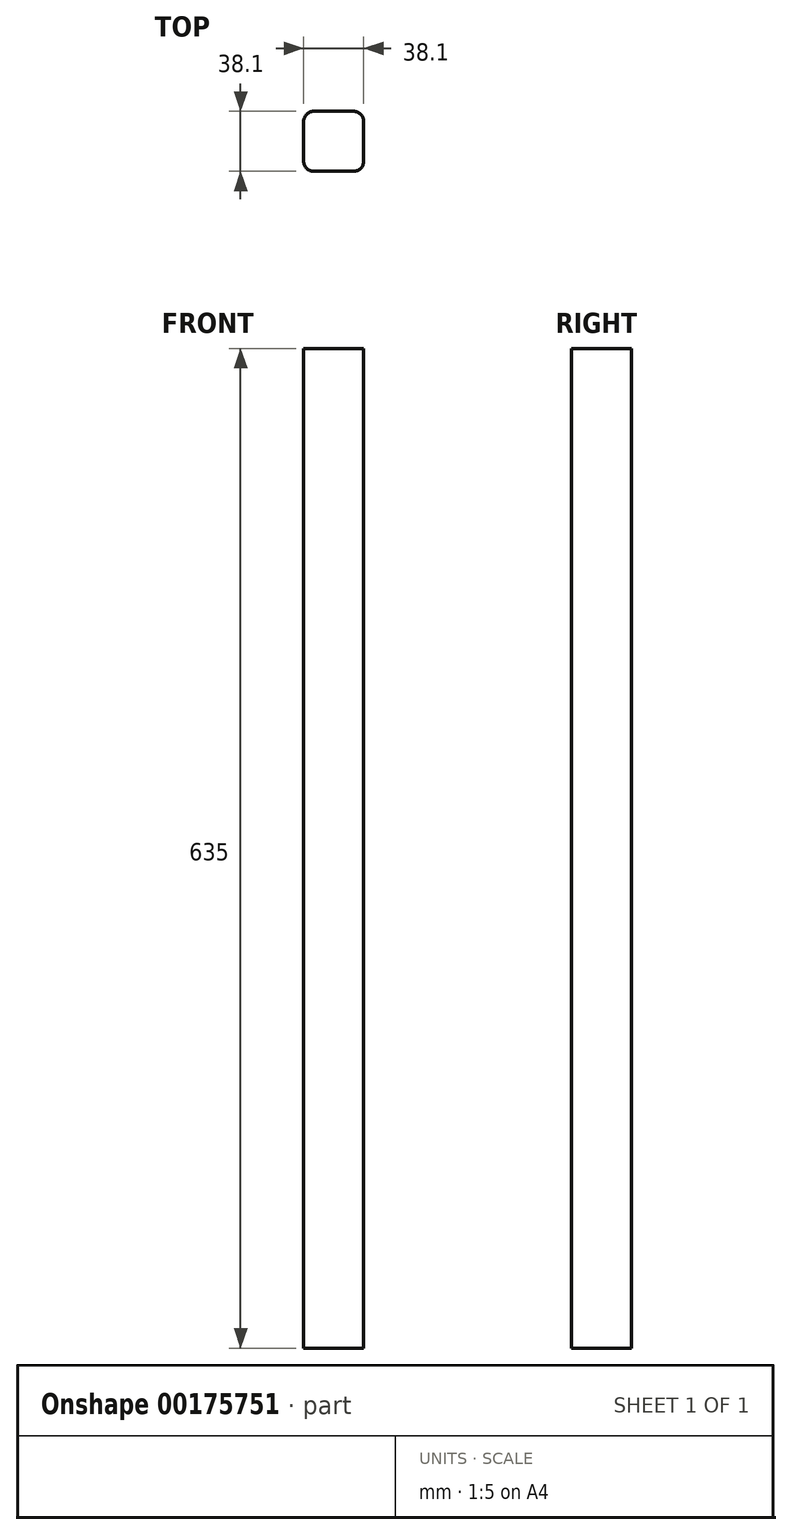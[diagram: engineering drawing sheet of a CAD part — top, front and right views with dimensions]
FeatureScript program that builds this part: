
annotation { "Feature Type Name" : "Feature", "Feature Type Description" : "" }
export const myFeature = defineFeature(function(context is Context, id is Id, definition is map)
    precondition{}
    {
        {
            var Q0;
            Q0=qCreatedBy(makeId("Top.planeOp"),FACE);
            var sketch = newSketch(context, id + "F0", { "sketchPlane" : qUnion([Q0])});
            skLineSegment(sketch, "E0.bottom", {"start": v(12.7, 19.05) * mm, "end": v(-12.7, 19.05) * mm});
            skLineSegment(sketch, "E0.top", {"start": v(12.7, -19.05) * mm, "end": v(-12.7, -19.05) * mm});
            skLineSegment(sketch, "E0.left", {"start": v(19.05, 12.7) * mm, "end": v(19.05, -12.7) * mm});
            skLineSegment(sketch, "E0.right", {"start": v(-19.05, 12.7) * mm, "end": v(-19.05, -12.7) * mm});
            skPoint(sketch, "E0.middle", {"position": v(0, 0) * mm});
            skPoint(sketch, "E1.visualSharp", {"position": v(19.05, 19.05) * mm});
            skArc(sketch, "E1.filletArc", {"start": v(19.05, 12.7) * mm, "mid": v(17.2, 17.2) * mm, "end": v(12.7, 19.05) * mm});
            skPoint(sketch, "E2.visualSharp", {"position": v(-19.05, 19.05) * mm});
            skArc(sketch, "E2.filletArc", {"start": v(-12.7, 19.05) * mm, "mid": v(-17.2, 17.2) * mm, "end": v(-19.05, 12.7) * mm});
            skPoint(sketch, "E3.visualSharp", {"position": v(-19.05, -19.05) * mm});
            skArc(sketch, "E3.filletArc", {"start": v(-19.05, -12.7) * mm, "mid": v(-17.2, -17.2) * mm, "end": v(-12.7, -19.05) * mm});
            skPoint(sketch, "E4.visualSharp", {"position": v(19.05, -19.05) * mm});
            skArc(sketch, "E4.filletArc", {"start": v(12.7, -19.05) * mm, "mid": v(17.2, -17.2) * mm, "end": v(19.05, -12.7) * mm});
            skSolve(sketch);
        }
        {
            var Q0;
            Q0=qSketchRegion(id+"F0",true);
            extrude(context, id + "F1", {"entities" : qUnion([Q0]), "depth" : 635 * mm});
        }
    });
